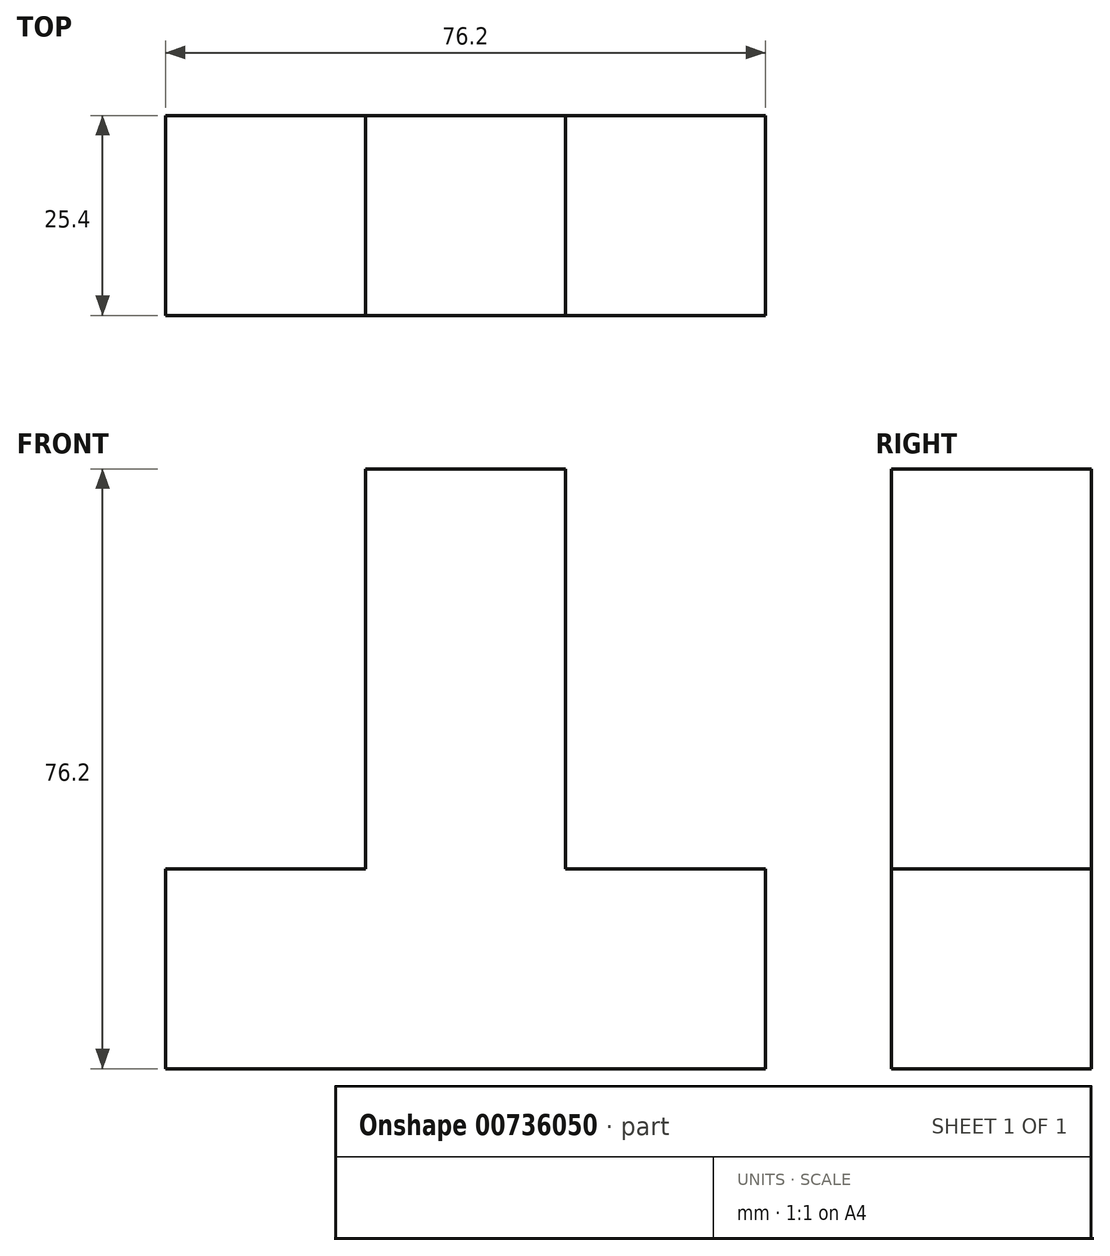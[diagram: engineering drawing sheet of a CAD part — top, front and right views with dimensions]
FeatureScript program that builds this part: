
annotation { "Feature Type Name" : "Feature", "Feature Type Description" : "" }
export const myFeature = defineFeature(function(context is Context, id is Id, definition is map)
    precondition{}
    {
        {
            var Q0;
            Q0=qCreatedBy(makeId("Front.planeOp"),FACE);
            var sketch = newSketch(context, id + "F0", { "sketchPlane" : qUnion([Q0])});
            skLineSegment(sketch, "E0", {"start": v(-50.8, 25.4) * mm, "end": v(-50.8, 0) * mm});
            skLineSegment(sketch, "E1", {"start": v(-50.8, 0) * mm, "end": v(25.4, 0) * mm});
            skLineSegment(sketch, "E2", {"start": v(25.4, 0) * mm, "end": v(25.4, 25.4) * mm});
            skLineSegment(sketch, "E3", {"start": v(25.4, 25.4) * mm, "end": v(0, 25.4) * mm});
            skLineSegment(sketch, "E4", {"start": v(-50.8, 25.4) * mm, "end": v(-25.4, 25.4) * mm});
            skLineSegment(sketch, "E5", {"start": v(0, 25.4) * mm, "end": v(0, 76.2) * mm});
            skLineSegment(sketch, "E6", {"start": v(-25.4, 25.4) * mm, "end": v(-25.4, 76.2) * mm});
            skLineSegment(sketch, "E7", {"start": v(-25.4, 76.2) * mm, "end": v(0, 76.2) * mm});
            skSolve(sketch);
        }
        {
            var Q0;
            Q0=qSketchRegion(id+"F0",true);
            extrude(context, id + "F1", {"entities" : qUnion([Q0]), "depth" : 25.4 * mm, "offsetDistance" : 25.4 * mm});
        }
    });
